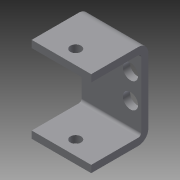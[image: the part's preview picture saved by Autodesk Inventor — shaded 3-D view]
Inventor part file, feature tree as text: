
AUTODESK INVENTOR PART (.ipt)
format: ipt  version: 2013 (Build 170138000, 138)  size: 134,656 bytes
history: native  units: in
note: dims shown in document units (in); Inventor stores cm internally (conversion verified against a paired STEP export)
features: sketch x5, sheet_metal_op x4, other x3, reference x2, extrude x1
ambient origin geometry x8: Origin, YZ Plane, XZ Plane, XY Plane, X Axis, Y Axis, Z Axis, Center Point
bodies: Solid1 (feature_tree)
feature tree (15):
  sheet_metal_op  "Face1"
  sheet_metal_op  "Flange1"
  extrude  "Extrusion1"  Depth=1.15in
  sketch  "Sketch8"  dims[d9=0.25in d10=0.125in d11=1.0in d12=90.0deg d13=0.05in d14=0.5in d15=0.125in d16=0.125in d17=0.25in d18=0.1875in d19=2999.0in d20=0.0in d21=0.575in d26=0.125in d27=0.0in]
  sketch  "Sketch1"  dims[d4=0.5788in d5=1.15in]
  other  "Plate1"
  sketch  "Sketch2"  dims[d6=0.125in]
  other  "Plate2"
  sheet_metal_op  "Bend1"
  sheet_metal_op  "Corner1"
  sketch  "Sketch3"  dims[d7=0.125in]
  sketch  "Sketch7"  dims[d8=0.0625in]
  reference  "Reference4"
  reference  "Reference5"
  other  "Cut3"
